# Revit family: VENTS-TT_SILENT_M_100_125_150_160
name_source: partatom
category: Mechanical Equipment
units: mm (PartAtom-declared; Revit-internal decimal feet)

## family parameters
Always vertical = No
Classification = None
Cut with Voids When Loaded = No
OmniClass Number = 23.75.35.17.11
OmniClass Title = Fans for Air Ductwork
Part Type = Breaks Into
Room Calculation Point = No
Round Connector Dimension = Use Diameter
Shared = No
Work Plane-Based = No

## types (8) — shared parameters
Current = 0 A
Dd12 = 3 mm  [stored 0.00984252 ft]
Dd22 = 3 mm  [stored 0.00984252 ft]
Description = Inline mixed-flow fan in sound- and heat-insulated casing for round ducts
Distribution Box Material = Distribution Box Dark Grey
ElBoxR = 15 mm  [stored 0.0492126 ft]
Family Version = 1.0
Fan Material = Metal Black
Hanger Material = Metal Zinc
HangerExtraL = Yes
HangerW = 93 mm  [stored 0.305118 ft]
L1 = 25 mm  [stored 0.082021 ft]
L12 = 8 mm  [stored 0.0262467 ft]
L13 = 13 mm
L16 = 8 mm  [stored 0.0262467 ft]
L17 = 6 mm  [stored 0.019685 ft]
L2 = 25 mm  [stored 0.082021 ft]
L22 = 8 mm  [stored 0.0262467 ft]
L23 = 13 mm
L26 = 8 mm  [stored 0.0262467 ft]
L27 = 6 mm  [stored 0.019685 ft]
Load Classification = HVAC
Maintenance Zone Height = 600 mm
Maintenance Zone Length = 600 mm
Maintenance Zone Length Calc = 600 mm
Maintenance Zone Material = Maintenance Zone
Maintenance Zone Width = 600 mm
Manufacturer = Vents
Number of Poles = 1
Power Factor = 1
Protection rating = IPX4
Transported Air Temperature (°C) = -25...+60
URL = https://ventilation-system.com
Voltage = 230 V

## per-type parameters (varying)
- TT Silent-M 100 (min): Apparent Power=24 VA; D=100 mm  [stored 0.328084 ft]; D1=214 mm; Dd13=4 mm  [stored 0.0131234 ft]; Dd14=39 mm  [stored 0.127953 ft]; Dd16=54 mm  [stored 0.177165 ft]; Dd23=4 mm  [stored 0.0131234 ft]; Dd24=39 mm  [stored 0.127953 ft]; Dd26=54 mm  [stored 0.177165 ft]; Duct Connection Size=100 mm  [stored 0.328084 ft]; ElBoxH=124 mm  [stored 0.406824 ft]; ElBoxL=98 mm  [stored 0.321522 ft]; ElBoxW=116 mm  [stored 0.380577 ft]; HangerBaseH=113 mm  [stored 0.370735 ft]; HangerH=113 mm  [stored 0.370735 ft]; HangerL=208 mm; HangerL1=208 mm; L=505 mm; L11=139 mm; L14=34 mm; L15=70 mm; L21=184 mm; L24=39 mm  [stored 0.127953 ft]; L25=110 mm; Maximum Air Flow=170 m³/h; Model=TT Silent-M 100; Noise Level at 3 m (dBa)=24; Power=24 W; R1=107 mm  [stored 0.35105 ft]; RPM (min-1)=2030; Type Comments=Inline mixed-flow fan TT Silent-M 100; Weight=4.60 kg
- TT Silent-M 100 (max): Apparent Power=26 VA; D=100 mm  [stored 0.328084 ft]; D1=214 mm; Dd13=4 mm  [stored 0.0131234 ft]; Dd14=39 mm  [stored 0.127953 ft]; Dd16=54 mm  [stored 0.177165 ft]; Dd23=4 mm  [stored 0.0131234 ft]; Dd24=39 mm  [stored 0.127953 ft]; Dd26=54 mm  [stored 0.177165 ft]; Duct Connection Size=100 mm  [stored 0.328084 ft]; ElBoxH=124 mm  [stored 0.406824 ft]; ElBoxL=98 mm  [stored 0.321522 ft]; ElBoxW=116 mm  [stored 0.380577 ft]; HangerBaseH=113 mm  [stored 0.370735 ft]; HangerH=113 mm  [stored 0.370735 ft]; HangerL=208 mm; HangerL1=208 mm; L=505 mm; L11=139 mm; L14=34 mm; L15=70 mm; L21=184 mm; L24=39 mm  [stored 0.127953 ft]; L25=110 mm; Maximum Air Flow=240 m³/h; Model=TT Silent-M 100; Noise Level at 3 m (dBa)=29; Power=26 W; R1=107 mm  [stored 0.35105 ft]; RPM (min-1)=2630; Type Comments=Inline mixed-flow fan TT Silent-M 100; Weight=4.60 kg
- TT Silent-M 125 (min): Apparent Power=25 VA; D=125 mm; D1=214 mm; Dd13=4 mm  [stored 0.0131234 ft]; Dd14=28 mm  [stored 0.0918635 ft]; Dd16=41 mm  [stored 0.134514 ft]; Dd23=4 mm  [stored 0.0131234 ft]; Dd24=26 mm  [stored 0.0853018 ft]; Dd26=41 mm  [stored 0.134514 ft]; Duct Connection Size=125 mm; ElBoxH=124 mm  [stored 0.406824 ft]; ElBoxL=98 mm  [stored 0.321522 ft]; ElBoxW=116 mm  [stored 0.380577 ft]; HangerBaseH=113 mm  [stored 0.370735 ft]; HangerH=113 mm  [stored 0.370735 ft]; HangerL=208 mm; HangerL1=208 mm; L=474 mm; L11=123 mm  [stored 0.403543 ft]; L14=24 mm  [stored 0.0787402 ft]; L15=64 mm  [stored 0.209974 ft]; L21=169 mm; L24=24 mm  [stored 0.0787402 ft]; L25=110 mm; Maximum Air Flow=230 m³/h; Model=TT Silent-M 125; Noise Level at 3 m (dBa)=23; Power=25 W; R1=107 mm  [stored 0.35105 ft]; RPM (min-1)=1650; Type Comments=Inline mixed-flow fan TT Silent-M 125; Weight=4.60 kg
- TT Silent-M 125 (max): Apparent Power=29 VA; D=125 mm; D1=214 mm; Dd13=4 mm  [stored 0.0131234 ft]; Dd14=28 mm  [stored 0.0918635 ft]; Dd16=41 mm  [stored 0.134514 ft]; Dd23=4 mm  [stored 0.0131234 ft]; Dd24=26 mm  [stored 0.0853018 ft]; Dd26=41 mm  [stored 0.134514 ft]; Duct Connection Size=125 mm; ElBoxH=124 mm  [stored 0.406824 ft]; ElBoxL=98 mm  [stored 0.321522 ft]; ElBoxW=116 mm  [stored 0.380577 ft]; HangerBaseH=113 mm  [stored 0.370735 ft]; HangerH=113 mm  [stored 0.370735 ft]; HangerL=208 mm; HangerL1=208 mm; L=474 mm; L11=123 mm  [stored 0.403543 ft]; L14=19 mm  [stored 0.062336 ft]; L15=69 mm; L21=169 mm; L24=24 mm  [stored 0.0787402 ft]; L25=110 mm; Maximum Air Flow=340 m³/h; Model=TT Silent-M 125; Noise Level at 3 m (dBa)=28; Power=29 W; R1=107 mm  [stored 0.35105 ft]; RPM (min-1)=2310; Type Comments=Inline mixed-flow fan TT Silent-M 125; Weight=4.60 kg
- TT Silent-M 150 (min): Apparent Power=45 VA; D=150 mm; D1=244 mm; Dd13=4 mm  [stored 0.0131234 ft]; Dd14=28 mm  [stored 0.0918635 ft]; Dd16=45 mm  [stored 0.147638 ft]; Dd23=4 mm  [stored 0.0131234 ft]; Dd24=22 mm  [stored 0.0721785 ft]; Dd26=44 mm  [stored 0.144357 ft]; Duct Connection Size=150 mm; ElBoxH=137 mm; ElBoxL=114 mm  [stored 0.374016 ft]; ElBoxW=150 mm; HangerBaseH=126 mm; HangerH=126 mm; HangerL=238 mm; HangerL1=238 mm; L=580 mm; L11=163 mm; L14=19 mm  [stored 0.062336 ft]; L15=109 mm; L21=209 mm; L24=11 mm  [stored 0.0360892 ft]; L25=163 mm; Maximum Air Flow=405 m³/h; Model=TT Silent-M 150; Noise Level at 3 m (dBa)=26; Power=45 W; R1=122 mm  [stored 0.400262 ft]; RPM (min-1)=1970; Type Comments=Inline mixed-flow fan TT Silent-M 150; Weight=6.10 kg
- TT Silent-M 150 (max): Apparent Power=52 VA; D=150 mm; D1=244 mm; Dd13=4 mm  [stored 0.0131234 ft]; Dd14=28 mm  [stored 0.0918635 ft]; Dd16=45 mm  [stored 0.147638 ft]; Dd23=4 mm  [stored 0.0131234 ft]; Dd24=22 mm  [stored 0.0721785 ft]; Dd26=44 mm  [stored 0.144357 ft]; Duct Connection Size=150 mm; ElBoxH=137 mm; ElBoxL=114 mm  [stored 0.374016 ft]; ElBoxW=150 mm; HangerBaseH=126 mm; HangerH=126 mm; HangerL=238 mm; HangerL1=238 mm; L=580 mm; L11=163 mm; L14=21 mm  [stored 0.0688976 ft]; L15=107 mm  [stored 0.35105 ft]; L21=209 mm; L24=11 mm  [stored 0.0360892 ft]; L25=163 mm; Maximum Air Flow=555 m³/h; Model=TT Silent-M 150; Noise Level at 3 m (dBa)=33; Power=52 W; R1=122 mm  [stored 0.400262 ft]; RPM (min-1)=2645; Type Comments=Inline mixed-flow fan TT Silent-M 150; Weight=6.10 kg
- TT Silent-M 160 (min): Apparent Power=45 VA; D=160 mm; D1=244 mm; Dd13=5 mm  [stored 0.0164042 ft]; Dd14=23 mm  [stored 0.0754593 ft]; Dd16=39 mm  [stored 0.127953 ft]; Dd23=5 mm  [stored 0.0164042 ft]; Dd24=17 mm; Dd26=39 mm  [stored 0.127953 ft]; Duct Connection Size=160 mm; ElBoxH=137 mm; ElBoxL=114 mm  [stored 0.374016 ft]; ElBoxW=150 mm; HangerBaseH=126 mm; HangerH=126 mm; HangerL=238 mm; HangerL1=238 mm; L=580 mm; L11=163 mm; L14=21 mm  [stored 0.0688976 ft]; L15=107 mm  [stored 0.35105 ft]; L21=209 mm; L24=11 mm  [stored 0.0360892 ft]; L25=163 mm; Maximum Air Flow=405 m³/h; Model=TT Silent-M 160; Noise Level at 3 m (dBa)=26; Power=45 W; R1=122 mm  [stored 0.400262 ft]; RPM (min-1)=1970; Type Comments=Inline mixed-flow fan TT Silent-M 160; Weight=6.10 kg
- TT Silent-M 160 (max): Apparent Power=52 VA; D=160 mm; D1=244 mm; Dd13=5 mm  [stored 0.0164042 ft]; Dd14=23 mm  [stored 0.0754593 ft]; Dd16=39 mm  [stored 0.127953 ft]; Dd23=5 mm  [stored 0.0164042 ft]; Dd24=17 mm; Dd26=39 mm  [stored 0.127953 ft]; Duct Connection Size=160 mm; ElBoxH=137 mm; ElBoxL=114 mm  [stored 0.374016 ft]; ElBoxW=150 mm; HangerBaseH=126 mm; HangerH=126 mm; HangerL=238 mm; HangerL1=238 mm; L=580 mm; L11=163 mm; L14=10 mm  [stored 0.0328084 ft]; L15=118 mm  [stored 0.387139 ft]; L21=209 mm; L24=11 mm  [stored 0.0360892 ft]; L25=163 mm; Maximum Air Flow=555 m³/h; Model=TT Silent-M 160; Noise Level at 3 m (dBa)=33; Power=52 W; R1=122 mm  [stored 0.400262 ft]; RPM (min-1)=2645; Type Comments=Inline mixed-flow fan TT Silent-M 160; Weight=6.10 kg

note: [stored X ft] marks values corroborated as IEEE doubles in the binary element streams (Revit-internal decimal feet)

## geometry (parser evidence)
native form markers: Sweep x9
no freeform markers — native parametric forms only
